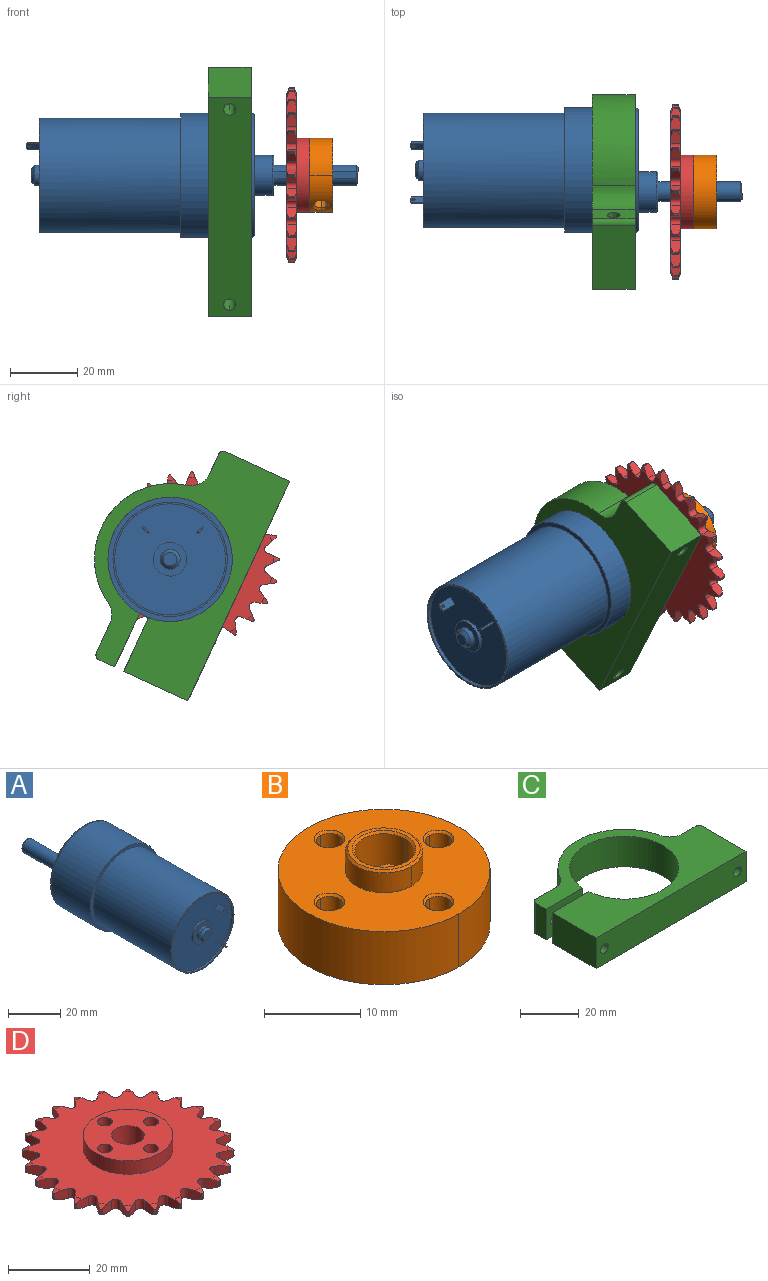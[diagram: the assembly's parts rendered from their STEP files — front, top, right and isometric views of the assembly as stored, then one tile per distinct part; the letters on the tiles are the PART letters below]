
ASSEMBLY  parts=4 mates=3
PART A: 37 faces, bbox 40.1x98.8x40.1 mm
  f0: cylinder r=3mm len=24.5mm, axis (0,-1,0), area 407.6mm2, adj f1,f3,f5
  f1: plane 24.5x2.16mm, normal (0,0,-1), area 53mm2, adj f0,f4,f5
  f2: plane 5x4.8mm, normal (0,1,0), area 19.4mm2, adj f3,f4
  f3: cone r=2.5mm half-angle=45deg, axis (0,-1,0), area 10.7mm2, adj f0,f2,f4
  f4: plane 2.17x0.51mm, normal (0,0.71,-0.71), area 1.5mm2, adj f1,f2,f3
  f5: plane 11x11mm, normal (0,1,0), area 67.1mm2, adj f0,f1,f36
  f6: plane 33x33mm, normal (0,-1,0), area 774.3mm2, adj f14,f15,f18,f19,f20,f21,f23,f24
  f7: plane 10x10mm, normal (0,-1,0), area 50.3mm2, adj f15,f16
  f8: plane 37x37mm, normal (0,-1,0), area 167.3mm2, adj f10,f12
  f9: plane 35x35mm, normal (0,1,0), area 849mm2, adj f11,f35
  f10: cylinder r=18.5mm len=37mm, axis (0,-1,0), area 2441mm2, adj f8,f35
  f11: cylinder r=6mm len=12mm, axis (0,-1,0), area 199.8mm2, adj f9,f36
  f12: cylinder r=17mm len=42mm, axis (0,1,0), area 4486.2mm2, adj f8,f13
  f13: plane 34x34mm, normal (0,-1,0), area 52.6mm2, adj f12,f14
  f14: cylinder r=16.5mm len=33mm, axis (0,-1,0), area 103.7mm2, adj f6,f13
  f15: cylinder r=5mm len=10mm, axis (0,1,0), area 31.4mm2, adj f6,f7
  f16: cylinder r=3mm len=6mm, axis (0,1,0), area 28.3mm2, adj f7,f30
  f17: plane 4x4mm, normal (0,-1,0), area 12.6mm2, adj f30
  f18: plane 4.5x0.35mm, normal (-0.71,0,-0.71), area 2.2mm2, adj f6,f19,f21,f33
  f19: plane 5x1.77mm, normal (0.71,0,-0.71), area 11.5mm2, adj f6,f18,f20,f22,f28,f33,f34
  f20: plane 4.5x0.35mm, normal (0.71,0,0.71), area 2.2mm2, adj f6,f19,f21,f34
  f21: plane 5x1.77mm, normal (-0.71,0,0.71), area 11.5mm2, adj f6,f18,f20,f22,f28,f33,f34
  f22: plane 1.41x1.41mm, normal (0,-1,0), area 0.8mm2, adj f19,f21,f33,f34
  f23: plane 4.5x0.35mm, normal (-0.71,0,0.71), area 2.3mm2, adj f6,f24,f26,f32
  f24: plane 5x1.77mm, normal (-0.71,0,-0.71), area 11.5mm2, adj f6,f23,f25,f27,f29,f31,f32
  f25: plane 4.5x0.35mm, normal (0.71,0,-0.71), area 2.2mm2, adj f6,f24,f26,f31
  f26: plane 5x1.77mm, normal (0.71,0,0.71), area 11.5mm2, adj f6,f23,f25,f27,f29,f31,f32
  f27: plane 1.41x1.41mm, normal (0,-1,0), area 0.7mm2, adj f24,f26,f31,f32
  f28: cylinder r=0.5mm len=1.06mm, axis (-0.71,0,0.71), area 1.6mm2, adj f19,f21
  f29: cylinder r=0.5mm len=1.06mm, axis (-0.71,0,-0.71), area 1.6mm2, adj f24,f26
  f30: cone r=2mm half-angle=45deg, axis (0,1,0), area 22.2mm2, adj f16,f17
  f31: plane 0.71x0.71mm, normal (0.5,-0.71,-0.5), area 0.4mm2, adj f24,f25,f26,f27
  f32: plane 0.71x0.71mm, normal (-0.5,-0.71,0.5), area 0.4mm2, adj f23,f24,f26,f27
  f33: plane 0.71x0.71mm, normal (-0.5,-0.71,-0.5), area 0.4mm2, adj f18,f19,f21,f22
  f34: plane 0.71x0.71mm, normal (0.5,-0.71,0.5), area 0.4mm2, adj f19,f20,f21,f22
  f35: torus R=17.5mm, axis (0,1,0), area 179mm2, adj f9,f10
  f36: torus R=5.5mm, axis (0,1,0), area 28.7mm2, adj f5,f11
PART B: 43 faces, bbox 22x22x9.5 mm
  f0: cylinder r=3.05mm len=9mm, axis (0,0,-1), area 85.7mm2, adj f1,f2,f4,f5,f6
  f1: cylinder r=3.05mm len=9mm, axis (0,0,-1), area 73.3mm2, adj f0,f3,f4,f5,f7
  f2: cone r=0mm half-angle=45deg, axis (0,0,1), area 3.5mm2, adj f0,f3,f8
  f3: cone r=0mm half-angle=45deg, axis (0,0,1), area 3.5mm2, adj f1,f2,f8
  f4: cylinder r=2.02mm len=8.72mm, axis (0.84,0.54,0), area 48.5mm2, adj f0,f1,f5,f17
  f5: cylinder r=2.02mm len=8.72mm, axis (0.84,0.54,0), area 48.5mm2, adj f0,f1,f4,f18
  f6: cone r=0mm half-angle=45deg, axis (0,0,-1), area 3.5mm2, adj f0,f7,f19
  f7: cone r=0mm half-angle=45deg, axis (0,0,-1), area 3.5mm2, adj f1,f6,f19
  f8: plane 7.52x7.5mm, normal (0,0,1), area 10mm2, adj f2,f3,f20,f21
  f9: cone r=0mm half-angle=45deg, axis (0,0,-1), area 1.6mm2, adj f10,f19,f22
  f10: cone r=0mm half-angle=45deg, axis (0,0,-1), area 1.6mm2, adj f9,f19,f23
  f11: cone r=0mm half-angle=45deg, axis (0,0,-1), area 1.6mm2, adj f12,f19,f24
  f12: cone r=0mm half-angle=45deg, axis (0,0,-1), area 1.6mm2, adj f11,f19,f25
  f13: cone r=0mm half-angle=45deg, axis (0,0,-1), area 1.6mm2, adj f14,f19,f26
  f14: cone r=0mm half-angle=45deg, axis (0,0,-1), area 1.6mm2, adj f13,f19,f27
  f15: cone r=0mm half-angle=45deg, axis (0,0,-1), area 1.6mm2, adj f16,f19,f28
  f16: cone r=0mm half-angle=45deg, axis (0,0,-1), area 1.6mm2, adj f15,f19,f29
  f17: bspline ~4.65x3.1mm, area 6.7mm2, adj f4,f18,f30
  f18: bspline ~4.65x3.1mm, area 6.7mm2, adj f5,f17,f30
  f19: plane 22.04x22mm, normal (0,0,-1), area 313.6mm2, adj f6,f7,f9,f10,f11,f12,f13,f14
  f20: cone r=0mm half-angle=45deg, axis (0,0,-1), area 4.3mm2, adj f8,f21,f32
  f21: cone r=0mm half-angle=45deg, axis (0,0,-1), area 4.3mm2, adj f8,f20,f33
  f22: cylinder r=1.35mm len=6.25mm, axis (0,0,-1), area 26.6mm2, adj f9,f23,f34
  f23: cylinder r=1.35mm len=6.25mm, axis (0,0,-1), area 26.6mm2, adj f10,f22,f35
  f24: cylinder r=1.35mm len=6.25mm, axis (0,0,-1), area 26.6mm2, adj f11,f25,f36
  f25: cylinder r=1.35mm len=6.25mm, axis (0,0,-1), area 26.6mm2, adj f12,f24,f37
  f26: cylinder r=1.35mm len=6.25mm, axis (0,0,-1), area 26.6mm2, adj f13,f27,f38
  f27: cylinder r=1.35mm len=6.25mm, axis (0,0,-1), area 26.6mm2, adj f14,f26,f39
  f28: cylinder r=1.35mm len=6.25mm, axis (0,0,-1), area 26.6mm2, adj f15,f29,f40
  f29: cylinder r=1.35mm len=6.25mm, axis (0,0,-1), area 26.6mm2, adj f16,f28,f41
  f30: cylinder r=11mm len=22mm, axis (0,0,1), area 210.3mm2, adj f17,f18,f19,f31,f42
  f31: cylinder r=11mm len=22mm, axis (0,0,1), area 233.3mm2, adj f19,f30,f42
  f32: cylinder r=4mm len=8mm, axis (0,0,1), area 31.4mm2, adj f20,f33,f42
  f33: cylinder r=4mm len=8mm, axis (0,0,1), area 31.4mm2, adj f21,f32,f42
  f34: cone r=0mm half-angle=45deg, axis (0,0,1), area 1.6mm2, adj f22,f35,f42
  f35: cone r=0mm half-angle=45deg, axis (0,0,1), area 1.6mm2, adj f23,f34,f42
  f36: cone r=0mm half-angle=45deg, axis (0,0,1), area 1.6mm2, adj f24,f37,f42
  f37: cone r=0mm half-angle=45deg, axis (0,0,1), area 1.6mm2, adj f25,f36,f42
  f38: cone r=0mm half-angle=45deg, axis (0,0,1), area 1.6mm2, adj f26,f39,f42
  f39: cone r=0mm half-angle=45deg, axis (0,0,1), area 1.6mm2, adj f27,f38,f42
  f40: cone r=0mm half-angle=45deg, axis (0,0,1), area 1.6mm2, adj f28,f41,f42
  f41: cone r=0mm half-angle=45deg, axis (0,0,1), area 1.6mm2, adj f29,f40,f42
  f42: plane 22.04x22mm, normal (0,0,1), area 297.6mm2, adj f30,f31,f32,f33,f34,f35,f36,f37
PART C: 22 faces, bbox 72x45x12.7 mm
  f0: cylinder r=1.85mm len=6.7mm, axis (0,-1,0), area 38.9mm2, adj f1,f12,f15
  f1: cylinder r=1.85mm len=6.7mm, axis (0,-1,0), area 38.9mm2, adj f0,f12,f15
  f2: cylinder r=1.85mm len=22.5mm, axis (0,-1,0), area 130.8mm2, adj f3,f8,f19
  f3: cylinder r=1.85mm len=22.5mm, axis (0,-1,0), area 130.8mm2, adj f2,f8,f19
  f4: cylinder r=1.85mm len=21mm, axis (0,-1,0), area 122.1mm2, adj f5,f17,f19
  f5: cylinder r=1.85mm len=21mm, axis (0,-1,0), area 122.1mm2, adj f4,f17,f19
  f6: plane 72x45.04mm, normal (0,0,1), area 1409.8mm2, adj f7,f8,f9,f10,f11,f12,f13,f14
  f7: cylinder r=1.5mm len=12.7mm, axis (0,0,-1), area 29.9mm2, adj f6,f8,f20,f21
  f8: plane 12.7x6.36mm, normal (0,1,0), area 70mm2, adj f2,f3,f6,f7,f9,f21
  f9: cylinder r=6.35mm len=12.7mm, axis (0,0,1), area 108.8mm2, adj f6,f8,f10,f21
  f10: cylinder r=22.5mm len=41.38mm, axis (0,0,1), area 683.2mm2, adj f6,f9,f11,f21
  f11: cylinder r=6.35mm len=12.7mm, axis (0,0,1), area 84mm2, adj f6,f10,f12,f21
  f12: plane 12.7x9.59mm, normal (0,1,0), area 111mm2, adj f0,f1,f6,f11,f13,f21
  f13: cylinder r=1.5mm len=12.7mm, axis (0,0,-1), area 29.9mm2, adj f6,f12,f14,f21
  f14: plane 12.7x5.2mm, normal (-1,0,0), area 66mm2, adj f6,f13,f15,f21
  f15: plane 17.56x12.7mm, normal (0,-1,0), area 212.3mm2, adj f0,f1,f6,f14,f16,f21
  f16: cylinder r=18.5mm len=37mm, axis (0,0,1), area 1438.1mm2, adj f6,f15,f17,f21
  f17: plane 17.56x12.7mm, normal (0,1,0), area 212.3mm2, adj f4,f5,f6,f16,f18,f21
  f18: plane 21x12.7mm, normal (-1,0,0), area 266.7mm2, adj f6,f17,f19,f21
  f19: plane 72x12.7mm, normal (0,-1,0), area 892.9mm2, adj f2,f3,f4,f5,f6,f18,f20,f21
  f20: plane 21x12.7mm, normal (1,0,0), area 266.7mm2, adj f6,f7,f19,f21
  f21: plane 72x45.04mm, normal (0,0,-1), area 1409.8mm2, adj f7,f8,f9,f10,f11,f12,f13,f14
PART D: 201 faces, bbox 52x52x6.8 mm
  f0: plane 48.65x48.65mm, normal (0,0,1), area 1311.2mm2, adj f1,f4,f7,f10,f13,f16,f19,f22
  f1: cone r=26mm half-angle=70deg, axis (0,0,-1), area 2.4mm2, adj f0,f2,f144,f146,f190,f193
  f2: cylinder r=26mm len=1.58mm, axis (0,0,1), area 0.5mm2, adj f1,f3,f190,f193
  f3: cone r=24.32mm half-angle=70deg, axis (0,0,1), area 2.4mm2, adj f2,f73,f144,f146,f190,f193
  f4: cone r=26mm half-angle=70deg, axis (0,0,-1), area 2.4mm2, adj f0,f5,f141,f143,f188,f191
  f5: cylinder r=26mm len=1.58mm, axis (0,0,1), area 0.5mm2, adj f4,f6,f188,f191
  f6: cone r=24.32mm half-angle=70deg, axis (0,0,1), area 2.4mm2, adj f5,f73,f141,f143,f188,f191
  f7: cone r=26mm half-angle=70deg, axis (0,0,-1), area 2.4mm2, adj f0,f8,f138,f140,f186,f189
  f8: cylinder r=26mm len=1.58mm, axis (0,0,1), area 0.5mm2, adj f7,f9,f186,f189
  f9: cone r=24.32mm half-angle=70deg, axis (0,0,1), area 2.4mm2, adj f8,f73,f138,f140,f186,f189
  f10: cone r=26mm half-angle=70deg, axis (0,0,-1), area 2.4mm2, adj f0,f11,f135,f137,f184,f187
  f11: cylinder r=26mm len=1.58mm, axis (0,0,1), area 0.5mm2, adj f10,f12,f184,f187
  f12: cone r=24.32mm half-angle=70deg, axis (0,0,1), area 2.4mm2, adj f11,f73,f135,f137,f184,f187
  f13: cone r=26mm half-angle=70deg, axis (0,0,-1), area 2.4mm2, adj f0,f14,f132,f134,f182,f185
  f14: cylinder r=26mm len=1.58mm, axis (0,0,1), area 0.5mm2, adj f13,f15,f182,f185
  f15: cone r=24.32mm half-angle=70deg, axis (0,0,1), area 2.4mm2, adj f14,f73,f132,f134,f182,f185
  f16: cone r=26mm half-angle=70deg, axis (0,0,-1), area 2.4mm2, adj f0,f17,f129,f131,f180,f183
  f17: cylinder r=26mm len=1.58mm, axis (0,0,1), area 0.5mm2, adj f16,f18,f180,f183
  f18: cone r=24.32mm half-angle=70deg, axis (0,0,1), area 2.4mm2, adj f17,f73,f129,f131,f180,f183
  f19: cone r=26mm half-angle=70deg, axis (0,0,-1), area 2.4mm2, adj f0,f20,f126,f128,f178,f181
  f20: cylinder r=26mm len=1.58mm, axis (0,0,1), area 0.5mm2, adj f19,f21,f178,f181
  f21: cone r=24.32mm half-angle=70deg, axis (0,0,1), area 2.4mm2, adj f20,f73,f126,f128,f178,f181
  f22: cone r=26mm half-angle=70deg, axis (0,0,-1), area 2.4mm2, adj f0,f23,f123,f125,f176,f179
  f23: cylinder r=26mm len=1.58mm, axis (0,0,1), area 0.5mm2, adj f22,f24,f176,f179
  f24: cone r=24.32mm half-angle=70deg, axis (0,0,1), area 2.4mm2, adj f23,f73,f123,f125,f176,f179
  f25: cone r=26mm half-angle=70deg, axis (0,0,-1), area 2.4mm2, adj f0,f26,f120,f122,f174,f177
  f26: cylinder r=26mm len=1.58mm, axis (0,0,1), area 0.5mm2, adj f25,f27,f174,f177
  f27: cone r=24.32mm half-angle=70deg, axis (0,0,1), area 2.4mm2, adj f26,f73,f120,f122,f174,f177
  f28: cone r=26mm half-angle=70deg, axis (0,0,-1), area 2.4mm2, adj f0,f29,f117,f119,f172,f175
  f29: cylinder r=26mm len=1.58mm, axis (0,0,1), area 0.5mm2, adj f28,f30,f172,f175
  f30: cone r=24.32mm half-angle=70deg, axis (0,0,1), area 2.4mm2, adj f29,f73,f117,f119,f172,f175
  f31: cone r=26mm half-angle=70deg, axis (0,0,-1), area 2.4mm2, adj f0,f32,f114,f116,f170,f173
  f32: cylinder r=26mm len=1.58mm, axis (0,0,1), area 0.5mm2, adj f31,f33,f170,f173
  f33: cone r=24.32mm half-angle=70deg, axis (0,0,1), area 2.4mm2, adj f32,f73,f114,f116,f170,f173
  f34: cone r=26mm half-angle=70deg, axis (0,0,-1), area 2.4mm2, adj f0,f35,f111,f113,f168,f171
  f35: cylinder r=26mm len=1.58mm, axis (0,0,1), area 0.5mm2, adj f34,f36,f168,f171
  f36: cone r=24.32mm half-angle=70deg, axis (0,0,1), area 2.4mm2, adj f35,f73,f111,f113,f168,f171
  f37: cone r=26mm half-angle=70deg, axis (0,0,-1), area 2.4mm2, adj f0,f38,f108,f110,f166,f169
  f38: cylinder r=26mm len=1.58mm, axis (0,0,1), area 0.5mm2, adj f37,f39,f166,f169
  f39: cone r=24.32mm half-angle=70deg, axis (0,0,1), area 2.4mm2, adj f38,f73,f108,f110,f166,f169
  f40: cone r=26mm half-angle=70deg, axis (0,0,-1), area 2.4mm2, adj f0,f41,f105,f107,f164,f167
  f41: cylinder r=26mm len=1.58mm, axis (0,0,1), area 0.5mm2, adj f40,f42,f164,f167
  f42: cone r=24.32mm half-angle=70deg, axis (0,0,1), area 2.4mm2, adj f41,f73,f105,f107,f164,f167
  f43: cone r=26mm half-angle=70deg, axis (0,0,-1), area 2.4mm2, adj f0,f44,f102,f104,f162,f165
  f44: cylinder r=26mm len=1.58mm, axis (0,0,1), area 0.5mm2, adj f43,f45,f162,f165
  f45: cone r=24.32mm half-angle=70deg, axis (0,0,1), area 2.4mm2, adj f44,f73,f102,f104,f162,f165
  f46: cone r=26mm half-angle=70deg, axis (0,0,-1), area 2.4mm2, adj f0,f47,f99,f101,f160,f163
  f47: cylinder r=26mm len=1.58mm, axis (0,0,1), area 0.5mm2, adj f46,f48,f160,f163
  f48: cone r=24.32mm half-angle=70deg, axis (0,0,1), area 2.4mm2, adj f47,f73,f99,f101,f160,f163
  f49: cone r=26mm half-angle=70deg, axis (0,0,-1), area 2.4mm2, adj f0,f50,f96,f98,f158,f161
  f50: cylinder r=26mm len=1.58mm, axis (0,0,1), area 0.5mm2, adj f49,f51,f158,f161
  f51: cone r=24.32mm half-angle=70deg, axis (0,0,1), area 2.4mm2, adj f50,f73,f96,f98,f158,f161
  f52: cone r=26mm half-angle=70deg, axis (0,0,-1), area 2.4mm2, adj f0,f53,f93,f95,f156,f159
  f53: cylinder r=26mm len=1.58mm, axis (0,0,1), area 0.5mm2, adj f52,f54,f156,f159
  f54: cone r=24.32mm half-angle=70deg, axis (0,0,1), area 2.4mm2, adj f53,f73,f93,f95,f156,f159
  f55: cone r=26mm half-angle=70deg, axis (0,0,-1), area 2.4mm2, adj f0,f56,f90,f92,f154,f157
  f56: cylinder r=26mm len=1.58mm, axis (0,0,1), area 0.5mm2, adj f55,f57,f154,f157
  f57: cone r=24.32mm half-angle=70deg, axis (0,0,1), area 2.4mm2, adj f56,f73,f90,f92,f154,f157
  f58: cone r=26mm half-angle=70deg, axis (0,0,-1), area 2.4mm2, adj f0,f59,f87,f89,f152,f155
  f59: cylinder r=26mm len=1.58mm, axis (0,0,1), area 0.5mm2, adj f58,f60,f152,f155
  f60: cone r=24.32mm half-angle=70deg, axis (0,0,1), area 2.4mm2, adj f59,f73,f87,f89,f152,f155
  f61: cone r=26mm half-angle=70deg, axis (0,0,-1), area 2.4mm2, adj f0,f62,f84,f86,f150,f153
  f62: cylinder r=26mm len=1.58mm, axis (0,0,1), area 0.5mm2, adj f61,f63,f150,f153
  f63: cone r=24.32mm half-angle=70deg, axis (0,0,1), area 2.4mm2, adj f62,f73,f84,f86,f150,f153
  f64: cone r=26mm half-angle=70deg, axis (0,0,-1), area 2.4mm2, adj f0,f65,f81,f83,f148,f151
  f65: cylinder r=26mm len=1.58mm, axis (0,0,1), area 0.5mm2, adj f64,f66,f148,f151
  f66: cone r=24.32mm half-angle=70deg, axis (0,0,1), area 2.4mm2, adj f65,f73,f81,f83,f148,f151
  f67: cone r=26mm half-angle=70deg, axis (0,0,-1), area 2.4mm2, adj f0,f68,f76,f77,f80,f149
  f68: cylinder r=26mm len=1.58mm, axis (0,0,1), area 0.5mm2, adj f67,f69,f77,f149
  f69: cone r=24.32mm half-angle=70deg, axis (0,0,1), area 2.4mm2, adj f68,f73,f76,f77,f80,f149
  f70: cone r=26mm half-angle=70deg, axis (0,0,-1), area 2.4mm2, adj f0,f71,f75,f78,f147,f192
  f71: cylinder r=26mm len=1.58mm, axis (0,0,1), area 0.5mm2, adj f70,f72,f78,f192
  f72: cone r=24.32mm half-angle=70deg, axis (0,0,1), area 2.4mm2, adj f71,f73,f75,f78,f147,f192
  f73: plane 48.65x48.65mm, normal (0,0,-1), area 1600.4mm2, adj f3,f6,f9,f12,f15,f18,f21,f24
  f74: cylinder r=1.25mm len=2.8mm, axis (0,0,1), area 7.2mm2, adj f0,f73,f75,f76
  f75: plane 2.99x2.8mm, normal (0.78,0.62,0), area 9.7mm2, adj f0,f70,f72,f73,f74,f78
  f76: plane 3.5x2.8mm, normal (-0.92,0.4,0), area 9.7mm2, adj f0,f67,f69,f73,f74,f77
  f77: cylinder r=0.2mm len=1.67mm, axis (0,0,1), area 0.4mm2, adj f67,f68,f69,f76
  f78: cylinder r=0.2mm len=1.67mm, axis (0,0,1), area 0.4mm2, adj f70,f71,f72,f75
  f79: cylinder r=1.25mm len=2.8mm, axis (0,0,1), area 7.2mm2, adj f0,f73,f80,f81
  f80: plane 3.5x2.8mm, normal (0.92,0.4,0), area 9.7mm2, adj f0,f67,f69,f73,f79,f149
  f81: plane 2.99x2.8mm, normal (-0.78,0.62,0), area 9.7mm2, adj f0,f64,f66,f73,f79,f148
  f82: cylinder r=1.25mm len=2.8mm, axis (0,0,1), area 7.2mm2, adj f0,f73,f83,f84
  f83: plane 3.77x2.8mm, normal (0.99,0.15,0), area 9.7mm2, adj f0,f64,f66,f73,f82,f151
  f84: plane 3.06x2.8mm, normal (-0.6,0.8,0), area 9.7mm2, adj f0,f61,f63,f73,f82,f150
  f85: cylinder r=1.25mm len=2.8mm, axis (0,0,1), area 7.2mm2, adj f0,f73,f86,f87
  f86: plane 3.79x2.8mm, normal (0.99,-0.12,0), area 9.7mm2, adj f0,f61,f63,f73,f85,f153
  f87: plane 3.54x2.8mm, normal (-0.37,0.93,0), area 9.7mm2, adj f0,f58,f60,f73,f85,f152
  f88: cylinder r=1.25mm len=2.8mm, axis (0,0,1), area 7.2mm2, adj f0,f73,f89,f90
  f89: plane 3.54x2.8mm, normal (0.93,-0.37,0), area 9.7mm2, adj f0,f58,f60,f73,f88,f155
  f90: plane 3.79x2.8mm, normal (-0.12,0.99,0), area 9.7mm2, adj f0,f55,f57,f73,f88,f154
  f91: cylinder r=1.25mm len=2.8mm, axis (0,0,1), area 7.2mm2, adj f0,f73,f92,f93
  f92: plane 3.06x2.8mm, normal (0.8,-0.6,0), area 9.7mm2, adj f0,f55,f57,f73,f91,f157
  f93: plane 3.77x2.8mm, normal (0.15,0.99,0), area 9.7mm2, adj f0,f52,f54,f73,f91,f156
  f94: cylinder r=1.25mm len=2.8mm, axis (0,0,1), area 7.2mm2, adj f0,f73,f95,f96
  f95: plane 2.99x2.8mm, normal (0.62,-0.78,0), area 9.7mm2, adj f0,f52,f54,f73,f94,f159
  f96: plane 3.5x2.8mm, normal (0.4,0.92,0), area 9.7mm2, adj f0,f49,f51,f73,f94,f158
  f97: cylinder r=1.25mm len=2.8mm, axis (0,0,1), area 7.2mm2, adj f0,f73,f98,f99
  f98: plane 3.5x2.8mm, normal (0.4,-0.92,0), area 9.7mm2, adj f0,f49,f51,f73,f97,f161
  f99: plane 2.99x2.8mm, normal (0.62,0.78,0), area 9.7mm2, adj f0,f46,f48,f73,f97,f160
  f100: cylinder r=1.25mm len=2.8mm, axis (0,0,1), area 7.2mm2, adj f0,f73,f101,f102
  f101: plane 3.77x2.8mm, normal (0.15,-0.99,0), area 9.7mm2, adj f0,f46,f48,f73,f100,f163
  f102: plane 3.06x2.8mm, normal (0.8,0.6,0), area 9.7mm2, adj f0,f43,f45,f73,f100,f162
  f103: cylinder r=1.25mm len=2.8mm, axis (0,0,1), area 7.2mm2, adj f0,f73,f104,f105
  f104: plane 3.79x2.8mm, normal (-0.12,-0.99,0), area 9.7mm2, adj f0,f43,f45,f73,f103,f165
  f105: plane 3.54x2.8mm, normal (0.93,0.37,0), area 9.7mm2, adj f0,f40,f42,f73,f103,f164
  f106: cylinder r=1.25mm len=2.8mm, axis (0,0,1), area 7.2mm2, adj f0,f73,f107,f108
  f107: plane 3.54x2.8mm, normal (-0.37,-0.93,0), area 9.7mm2, adj f0,f40,f42,f73,f106,f167
  f108: plane 3.79x2.8mm, normal (0.99,0.12,0), area 9.7mm2, adj f0,f37,f39,f73,f106,f166
  f109: cylinder r=1.25mm len=2.8mm, axis (0,0,1), area 7.2mm2, adj f0,f73,f110,f111
  f110: plane 3.06x2.8mm, normal (-0.6,-0.8,0), area 9.7mm2, adj f0,f37,f39,f73,f109,f169
  f111: plane 3.77x2.8mm, normal (0.99,-0.15,0), area 9.7mm2, adj f0,f34,f36,f73,f109,f168
  f112: cylinder r=1.25mm len=2.8mm, axis (0,0,1), area 7.2mm2, adj f0,f73,f113,f114
  f113: plane 2.99x2.8mm, normal (-0.78,-0.62,0), area 9.7mm2, adj f0,f34,f36,f73,f112,f171
  f114: plane 3.5x2.8mm, normal (0.92,-0.4,0), area 9.7mm2, adj f0,f31,f33,f73,f112,f170
  f115: cylinder r=1.25mm len=2.8mm, axis (0,0,1), area 7.2mm2, adj f0,f73,f116,f117
  f116: plane 3.5x2.8mm, normal (-0.92,-0.4,0), area 9.7mm2, adj f0,f31,f33,f73,f115,f173
  f117: plane 2.99x2.8mm, normal (0.78,-0.62,0), area 9.7mm2, adj f0,f28,f30,f73,f115,f172
  f118: cylinder r=1.25mm len=2.8mm, axis (0,0,1), area 7.2mm2, adj f0,f73,f119,f120
  f119: plane 3.77x2.8mm, normal (-0.99,-0.15,0), area 9.7mm2, adj f0,f28,f30,f73,f118,f175
  f120: plane 3.06x2.8mm, normal (0.6,-0.8,0), area 9.7mm2, adj f0,f25,f27,f73,f118,f174
  f121: cylinder r=1.25mm len=2.8mm, axis (0,0,1), area 7.2mm2, adj f0,f73,f122,f123
  f122: plane 3.79x2.8mm, normal (-0.99,0.12,0), area 9.7mm2, adj f0,f25,f27,f73,f121,f177
  f123: plane 3.54x2.8mm, normal (0.37,-0.93,0), area 9.7mm2, adj f0,f22,f24,f73,f121,f176
  f124: cylinder r=1.25mm len=2.8mm, axis (0,0,1), area 7.2mm2, adj f0,f73,f125,f126
  f125: plane 3.54x2.8mm, normal (-0.93,0.37,0), area 9.7mm2, adj f0,f22,f24,f73,f124,f179
  f126: plane 3.79x2.8mm, normal (0.12,-0.99,0), area 9.7mm2, adj f0,f19,f21,f73,f124,f178
  f127: cylinder r=1.25mm len=2.8mm, axis (0,0,1), area 7.2mm2, adj f0,f73,f128,f129
  f128: plane 3.06x2.8mm, normal (-0.8,0.6,0), area 9.7mm2, adj f0,f19,f21,f73,f127,f181
  f129: plane 3.77x2.8mm, normal (-0.15,-0.99,0), area 9.7mm2, adj f0,f16,f18,f73,f127,f180
  f130: cylinder r=1.25mm len=2.8mm, axis (0,0,1), area 7.2mm2, adj f0,f73,f131,f132
  f131: plane 2.99x2.8mm, normal (-0.62,0.78,0), area 9.7mm2, adj f0,f16,f18,f73,f130,f183
  f132: plane 3.5x2.8mm, normal (-0.4,-0.92,0), area 9.7mm2, adj f0,f13,f15,f73,f130,f182
  f133: cylinder r=1.25mm len=2.8mm, axis (0,0,1), area 7.2mm2, adj f0,f73,f134,f135
  f134: plane 3.5x2.8mm, normal (-0.4,0.92,0), area 9.7mm2, adj f0,f13,f15,f73,f133,f185
  f135: plane 2.99x2.8mm, normal (-0.62,-0.78,0), area 9.7mm2, adj f0,f10,f12,f73,f133,f184
  f136: cylinder r=1.25mm len=2.8mm, axis (0,0,1), area 7.2mm2, adj f0,f73,f137,f138
  f137: plane 3.77x2.8mm, normal (-0.15,0.99,0), area 9.7mm2, adj f0,f10,f12,f73,f136,f187
  f138: plane 3.06x2.8mm, normal (-0.8,-0.6,0), area 9.7mm2, adj f0,f7,f9,f73,f136,f186
  f139: cylinder r=1.25mm len=2.8mm, axis (0,0,1), area 7.2mm2, adj f0,f73,f140,f141
  f140: plane 3.79x2.8mm, normal (0.12,0.99,0), area 9.7mm2, adj f0,f7,f9,f73,f139,f189
  f141: plane 3.54x2.8mm, normal (-0.93,-0.37,0), area 9.7mm2, adj f0,f4,f6,f73,f139,f188
  f142: cylinder r=1.25mm len=2.8mm, axis (0,0,1), area 7.2mm2, adj f0,f73,f143,f144
  f143: plane 3.54x2.8mm, normal (0.37,0.93,0), area 9.7mm2, adj f0,f4,f6,f73,f142,f191
  f144: plane 3.79x2.8mm, normal (-0.99,-0.12,0), area 9.7mm2, adj f0,f1,f3,f73,f142,f190
  f145: cylinder r=1.25mm len=2.8mm, axis (0,0,1), area 7.2mm2, adj f0,f73,f146,f147
  f146: plane 3.06x2.8mm, normal (0.6,0.8,0), area 9.7mm2, adj f0,f1,f3,f73,f145,f193
  f147: plane 3.77x2.8mm, normal (-0.99,0.15,0), area 9.7mm2, adj f0,f70,f72,f73,f145,f192
  f148: cylinder r=0.2mm len=1.67mm, axis (0,0,1), area 0.4mm2, adj f64,f65,f66,f81
  f149: cylinder r=0.2mm len=1.67mm, axis (0,0,1), area 0.4mm2, adj f67,f68,f69,f80
  f150: cylinder r=0.2mm len=1.67mm, axis (0,0,1), area 0.4mm2, adj f61,f62,f63,f84
  f151: cylinder r=0.2mm len=1.67mm, axis (0,0,1), area 0.4mm2, adj f64,f65,f66,f83
  f152: cylinder r=0.2mm len=1.67mm, axis (0,0,1), area 0.4mm2, adj f58,f59,f60,f87
  f153: cylinder r=0.2mm len=1.67mm, axis (0,0,1), area 0.4mm2, adj f61,f62,f63,f86
  f154: cylinder r=0.2mm len=1.67mm, axis (0,0,1), area 0.4mm2, adj f55,f56,f57,f90
  f155: cylinder r=0.2mm len=1.67mm, axis (0,0,1), area 0.4mm2, adj f58,f59,f60,f89
  f156: cylinder r=0.2mm len=1.67mm, axis (0,0,1), area 0.4mm2, adj f52,f53,f54,f93
  f157: cylinder r=0.2mm len=1.67mm, axis (0,0,1), area 0.4mm2, adj f55,f56,f57,f92
  f158: cylinder r=0.2mm len=1.67mm, axis (0,0,1), area 0.4mm2, adj f49,f50,f51,f96
  f159: cylinder r=0.2mm len=1.67mm, axis (0,0,1), area 0.4mm2, adj f52,f53,f54,f95
  f160: cylinder r=0.2mm len=1.67mm, axis (0,0,1), area 0.4mm2, adj f46,f47,f48,f99
  f161: cylinder r=0.2mm len=1.67mm, axis (0,0,1), area 0.4mm2, adj f49,f50,f51,f98
  f162: cylinder r=0.2mm len=1.67mm, axis (0,0,1), area 0.4mm2, adj f43,f44,f45,f102
  f163: cylinder r=0.2mm len=1.67mm, axis (0,0,1), area 0.4mm2, adj f46,f47,f48,f101
  f164: cylinder r=0.2mm len=1.67mm, axis (0,0,1), area 0.4mm2, adj f40,f41,f42,f105
  f165: cylinder r=0.2mm len=1.67mm, axis (0,0,1), area 0.4mm2, adj f43,f44,f45,f104
  f166: cylinder r=0.2mm len=1.67mm, axis (0,0,1), area 0.4mm2, adj f37,f38,f39,f108
  f167: cylinder r=0.2mm len=1.67mm, axis (0,0,1), area 0.4mm2, adj f40,f41,f42,f107
  f168: cylinder r=0.2mm len=1.67mm, axis (0,0,1), area 0.4mm2, adj f34,f35,f36,f111
  f169: cylinder r=0.2mm len=1.67mm, axis (0,0,1), area 0.4mm2, adj f37,f38,f39,f110
  f170: cylinder r=0.2mm len=1.67mm, axis (0,0,1), area 0.4mm2, adj f31,f32,f33,f114
  f171: cylinder r=0.2mm len=1.67mm, axis (0,0,1), area 0.4mm2, adj f34,f35,f36,f113
  f172: cylinder r=0.2mm len=1.67mm, axis (0,0,1), area 0.4mm2, adj f28,f29,f30,f117
  f173: cylinder r=0.2mm len=1.67mm, axis (0,0,1), area 0.4mm2, adj f31,f32,f33,f116
  f174: cylinder r=0.2mm len=1.67mm, axis (0,0,1), area 0.4mm2, adj f25,f26,f27,f120
  f175: cylinder r=0.2mm len=1.67mm, axis (0,0,1), area 0.4mm2, adj f28,f29,f30,f119
  f176: cylinder r=0.2mm len=1.67mm, axis (0,0,1), area 0.4mm2, adj f22,f23,f24,f123
  f177: cylinder r=0.2mm len=1.67mm, axis (0,0,1), area 0.4mm2, adj f25,f26,f27,f122
  f178: cylinder r=0.2mm len=1.67mm, axis (0,0,1), area 0.4mm2, adj f19,f20,f21,f126
  f179: cylinder r=0.2mm len=1.67mm, axis (0,0,1), area 0.4mm2, adj f22,f23,f24,f125
  f180: cylinder r=0.2mm len=1.67mm, axis (0,0,1), area 0.4mm2, adj f16,f17,f18,f129
  f181: cylinder r=0.2mm len=1.67mm, axis (0,0,1), area 0.4mm2, adj f19,f20,f21,f128
  f182: cylinder r=0.2mm len=1.67mm, axis (0,0,1), area 0.4mm2, adj f13,f14,f15,f132
  f183: cylinder r=0.2mm len=1.67mm, axis (0,0,1), area 0.4mm2, adj f16,f17,f18,f131
  f184: cylinder r=0.2mm len=1.67mm, axis (0,0,1), area 0.4mm2, adj f10,f11,f12,f135
  f185: cylinder r=0.2mm len=1.67mm, axis (0,0,1), area 0.4mm2, adj f13,f14,f15,f134
  f186: cylinder r=0.2mm len=1.67mm, axis (0,0,1), area 0.4mm2, adj f7,f8,f9,f138
  f187: cylinder r=0.2mm len=1.67mm, axis (0,0,1), area 0.4mm2, adj f10,f11,f12,f137
  f188: cylinder r=0.2mm len=1.67mm, axis (0,0,1), area 0.4mm2, adj f4,f5,f6,f141
  f189: cylinder r=0.2mm len=1.67mm, axis (0,0,1), area 0.4mm2, adj f7,f8,f9,f140
  f190: cylinder r=0.2mm len=1.67mm, axis (0,0,1), area 0.4mm2, adj f1,f2,f3,f144
  f191: cylinder r=0.2mm len=1.67mm, axis (0,0,1), area 0.4mm2, adj f4,f5,f6,f143
  f192: cylinder r=0.2mm len=1.67mm, axis (0,0,1), area 0.4mm2, adj f70,f71,f72,f147
  f193: cylinder r=0.2mm len=1.67mm, axis (0,0,1), area 0.4mm2, adj f1,f2,f3,f146
  f194: cylinder r=11mm len=22mm, axis (0,0,-1), area 276.5mm2, adj f0,f195
  f195: plane 22x22mm, normal (0,0,1), area 289.2mm2, adj f194,f196,f197,f198,f199,f200
  f196: cylinder r=4mm len=8mm, axis (0,0,1), area 170.9mm2, adj f73,f195
  f197: cylinder r=1.8mm len=6.8mm, axis (0,0,1), area 76.9mm2, adj f73,f195
  f198: cylinder r=1.8mm len=6.8mm, axis (0,0,1), area 76.9mm2, adj f73,f195
  f199: cylinder r=1.8mm len=6.8mm, axis (0,0,1), area 76.9mm2, adj f73,f195
  f200: cylinder r=1.8mm len=6.8mm, axis (0,0,1), area 76.9mm2, adj f73,f195
PLACE A rot(axis=(-0.58,-0.58,-0.58),120deg) t=(494.62,461.44,-454.45)mm
PLACE B rot(axis=(0.71,0,-0.71),180deg) t=(533.09,454.94,-454.45)mm
PLACE C rot(axis=(0.21,-0.95,-0.21),92.6deg) t=(509.27,461.44,-454.45)mm
PLACE D rot(axis=(0,1,0),90deg) t=(529.09,454.94,-454.45)mm
MATE revolute A.f10 <-> C.f10  axis (-1,0,0) through (515.62,461.44,-454.45)mm
MATE fastened B.f20 <-> D.f1  axis (-1,0,0) through (533.09,454.94,-454.45)mm
MATE slider B.f20 <-> A.f0  axis (1,0,0) through (539.84,454.94,-454.45)mm
